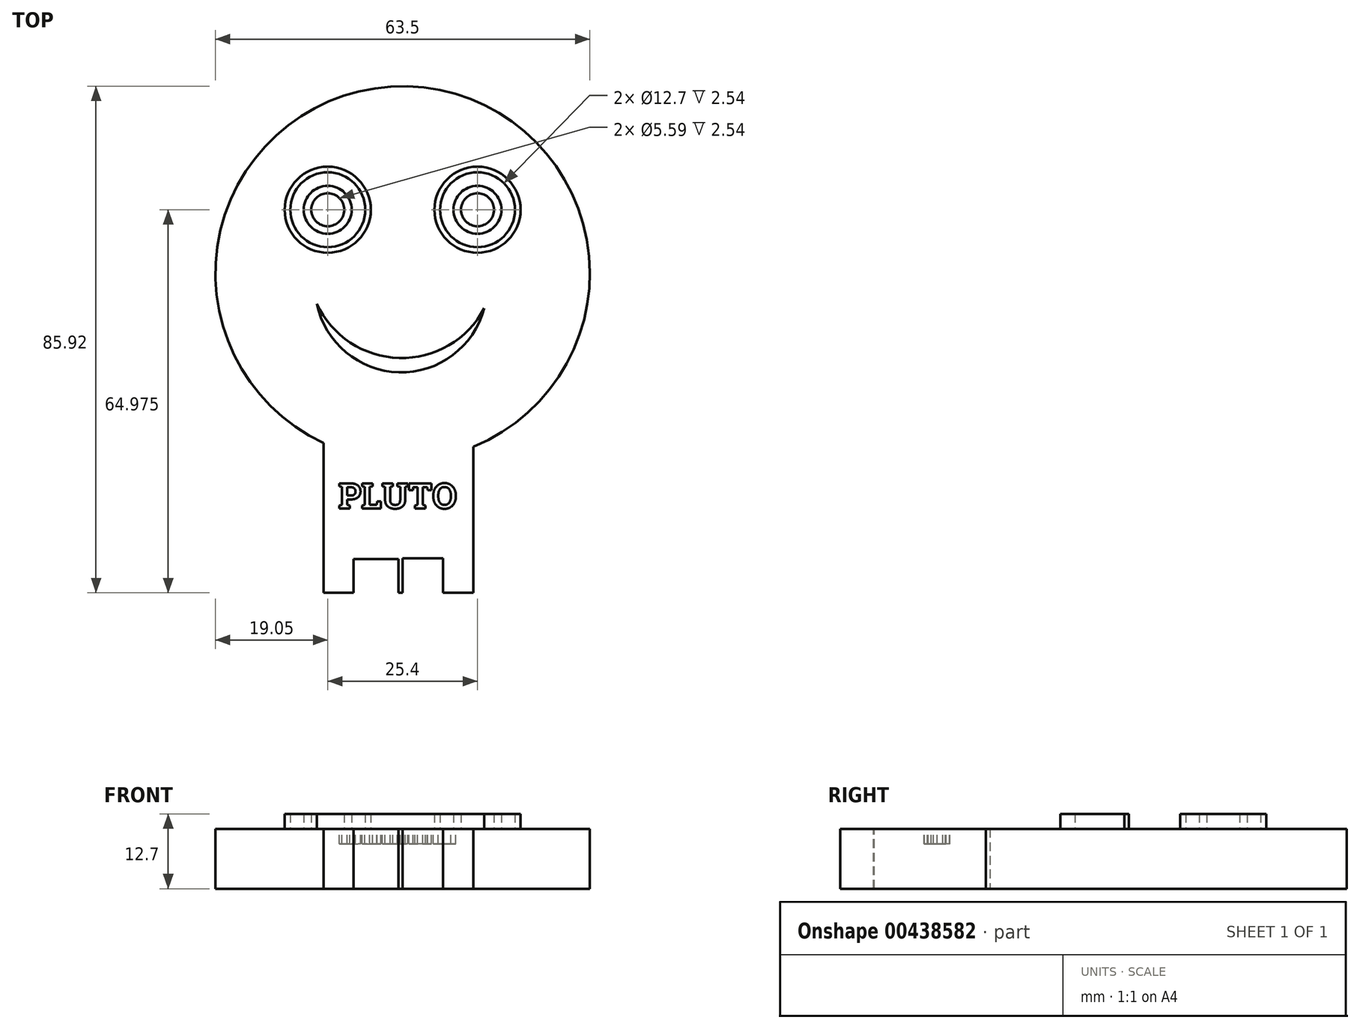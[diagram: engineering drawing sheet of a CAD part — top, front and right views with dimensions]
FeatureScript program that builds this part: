
annotation { "Feature Type Name" : "Feature", "Feature Type Description" : "" }
export const myFeature = defineFeature(function(context is Context, id is Id, definition is map)
    precondition{}
    {
        {
            var Q0;
            Q0=qCreatedBy(makeId("Top.planeOp"),FACE);
            var sketch = newSketch(context, id + "F0", { "sketchPlane" : qUnion([Q0])});
            skCircle(sketch, "E0", {"center": v(0, 20.55) * mm, "radius": 31.75 * mm});
            skLineSegment(sketch, "E1.bottom", {"start": v(-13.44, -8.22) * mm, "end": v(11.96, -8.22) * mm});
            skLineSegment(sketch, "E1.top", {"start": v(-13.44, -33.62) * mm, "end": v(11.96, -33.62) * mm});
            skLineSegment(sketch, "E1.left", {"start": v(-13.44, -8.22) * mm, "end": v(-13.44, -33.62) * mm});
            skLineSegment(sketch, "E1.right", {"start": v(11.96, -8.22) * mm, "end": v(11.96, -33.62) * mm});
            skSolve(sketch);
        }
        {
            var Q0;
            {var subQ0=sQuery(id+"F0.wireOp",EDGE,"E1.bottom");Q0=makeQuery(id+"F0.imprint","IMPRINT",FACE,{"disambiguationData":[TD([[makeQuery(id+"F0.imprint","IMPRINT",EDGE,{"derivedFrom":subQ0}),-1.0]])]});}
            var Q1;
            {var subQ4=sQuery(id+"F0.wireOp",EDGE,"E1.top");Q1=makeQuery(id+"F0.imprint","IMPRINT",FACE,{"disambiguationData":[TD([[makeQuery(id+"F0.imprint","IMPRINT",EDGE,{"derivedFrom":subQ4}),1.0]])]});}
            var Q2;
            {var subQ0=sQuery(id+"F0.wireOp",EDGE,"E1.bottom");Q2=makeQuery(id+"F0.imprint","IMPRINT",FACE,{"disambiguationData":[TD([[makeQuery(id+"F0.imprint","IMPRINT",EDGE,{"derivedFrom":subQ0}),1.0]])]});}
            extrude(context, id + "F1", {"entities" : qUnion([Q0, Q1, Q2]), "depth" : 10.16 * mm});
        }
        {
            var Q0;
            Q0=makeQuery(id+"F1.opExtrude","CAP_FACE",FACE,{"disambiguationData":[OSD([sQuery(id+"F0.wireOp",EDGE,"E0"),sQuery(id+"F0.wireOp",EDGE,"E1.top"),sQuery(id+"F0.wireOp",EDGE,"E1.left"),sQuery(id+"F0.wireOp",EDGE,"E1.right")])],"isStart":false});
            var sketch = newSketch(context, id + "F2", { "sketchPlane" : qUnion([Q0])});
            skCircle(sketch, "E2", {"center": v(-12.7, 31.35) * mm, "radius": 6.35 * mm});
            skCircle(sketch, "E3", {"center": v(12.7, 31.35) * mm, "radius": 6.35 * mm});
            skArc(sketch, "E4", {"start": v(-14.54, 15.4) * mm, "mid": v(-0.65, 3.78) * mm, "end": v(13.85, 14.63) * mm});
            skLineSegment(sketch, "E5", {"start": v(-12.7, 31.35) * mm, "end": v(0, 31.35) * mm, "construction": true});
            skLineSegment(sketch, "E6", {"start": v(0, 31.35) * mm, "end": v(12.7, 31.35) * mm, "construction": true});
            skCircle(sketch, "E7", {"center": v(-12.7, 31.35) * mm, "radius": 7.3 * mm});
            skCircle(sketch, "E8", {"center": v(12.7, 31.35) * mm, "radius": 7.3 * mm});
            skArc(sketch, "E9", {"start": v(-14.54, 15.4) * mm, "mid": v(-0.58, 6.21) * mm, "end": v(13.85, 14.63) * mm});
            skSolve(sketch);
        }
        {
            var Q0;
            Q0=makeQuery(id+"F2.imprint","IMPRINT",FACE,{"disambiguationData":[TD([[makeQuery(id+"F2.imprint","IMPRINT",EDGE,{"derivedFrom":sQuery(id+"F2.wireOp",EDGE,"E2")}),-1.0]])]});
            var Q1;
            Q1=makeQuery(id+"F2.imprint","IMPRINT",FACE,{"disambiguationData":[TD([[makeQuery(id+"F2.imprint","IMPRINT",EDGE,{"derivedFrom":sQuery(id+"F2.wireOp",EDGE,"E4")}),1.0]])]});
            var Q2;
            Q2=makeQuery(id+"F2.imprint","IMPRINT",FACE,{"disambiguationData":[TD([[makeQuery(id+"F2.imprint","IMPRINT",EDGE,{"derivedFrom":sQuery(id+"F2.wireOp",EDGE,"E3")}),-1.0]])]});
            var Q3;
            Q3=sQuery(id+"F2.wireOp",EDGE,"E2");
            var Q4;
            Q4=sQuery(id+"F2.wireOp",EDGE,"E7");
            extrude(context, id + "F3", {"entities" : qUnion([Q0, Q1, Q2]), "operationType" : NewBodyOperationType.ADD, "surfaceEntities" : qUnion([Q3, Q4]), "depth" : 2.54 * mm});
        }
        {
            var Q0;
            Q0=makeQuery(id+"F1.opExtrude","CAP_FACE",FACE,{"disambiguationData":[OSD([sQuery(id+"F0.wireOp",EDGE,"E0"),sQuery(id+"F0.wireOp",EDGE,"E1.top"),sQuery(id+"F0.wireOp",EDGE,"E1.left"),sQuery(id+"F0.wireOp",EDGE,"E1.right")])],"isStart":false});
            var sketch = newSketch(context, id + "F4", { "sketchPlane" : qUnion([Q0])});
            skCircle(sketch, "E10", {"center": v(-12.7, 31.35) * mm, "radius": 2.8 * mm});
            skCircle(sketch, "E11", {"center": v(12.7, 31.35) * mm, "radius": 2.8 * mm});
            skLineSegment(sketch, "E12", {"start": v(-12.7, 31.35) * mm, "end": v(0, 31.35) * mm, "construction": true});
            skLineSegment(sketch, "E13", {"start": v(12.7, 31.35) * mm, "end": v(0, 31.35) * mm, "construction": true});
            skCircle(sketch, "E14", {"center": v(-12.7, 31.35) * mm, "radius": 4.06 * mm});
            skCircle(sketch, "E15", {"center": v(12.7, 31.35) * mm, "radius": 4.06 * mm});
            skSolve(sketch);
        }
        {
            var Q0;
            Q0=makeQuery(id+"F4.imprint","IMPRINT",FACE,{"disambiguationData":[TD([[makeQuery(id+"F4.imprint","IMPRINT",EDGE,{"derivedFrom":sQuery(id+"F4.wireOp",EDGE,"E10")}),-1.0]])]});
            var Q1;
            Q1=makeQuery(id+"F4.imprint","IMPRINT",FACE,{"disambiguationData":[TD([[makeQuery(id+"F4.imprint","IMPRINT",EDGE,{"derivedFrom":sQuery(id+"F4.wireOp",EDGE,"E11")}),-1.0]])]});
            extrude(context, id + "F5", {"entities" : qUnion([Q0, Q1]), "operationType" : NewBodyOperationType.ADD, "depth" : 2.54 * mm});
        }
        {
            var Q0;
            Q0=makeQuery(id+"F1.opExtrude","CAP_FACE",FACE,{"disambiguationData":[OSD([sQuery(id+"F0.wireOp",EDGE,"E0"),sQuery(id+"F0.wireOp",EDGE,"E1.top"),sQuery(id+"F0.wireOp",EDGE,"E1.left"),sQuery(id+"F0.wireOp",EDGE,"E1.right")])],"isStart":false});
            var sketch = newSketch(context, id + "F6", { "sketchPlane" : qUnion([Q0])});
            skPoint(sketch, "E16.oppositeSnap0", {"position": v(-0.74, -33.62) * mm});
            skLineSegment(sketch, "E16.bottom", {"start": v(-8.34, -27.92) * mm, "end": v(-0.74, -27.92) * mm});
            skLineSegment(sketch, "E16.top", {"start": v(-8.34, -46.63) * mm, "end": v(-0.74, -46.63) * mm});
            skLineSegment(sketch, "E16.left", {"start": v(-8.34, -27.92) * mm, "end": v(-8.34, -46.63) * mm});
            skLineSegment(sketch, "E16.right", {"start": v(-0.74, -27.92) * mm, "end": v(-0.74, -46.63) * mm});
            skLineSegment(sketch, "E17.bottom", {"start": v(0, -47.09) * mm, "end": v(6.88, -47.09) * mm});
            skLineSegment(sketch, "E17.top", {"start": v(0, -27.8) * mm, "end": v(6.88, -27.8) * mm});
            skLineSegment(sketch, "E17.left", {"start": v(0, -47.09) * mm, "end": v(0, -27.8) * mm});
            skLineSegment(sketch, "E17.right", {"start": v(6.88, -47.09) * mm, "end": v(6.88, -27.8) * mm});
            skSolve(sketch);
        }
        {
            var Q0;
            Q0 = qSketchRegion(id + "F6", true);
            extrude(context, id + "F7", {"entities" : qUnion([Q0]), "operationType" : NewBodyOperationType.REMOVE, "oppositeDirection" : true, "depth" : 25.4 * mm});
        }
        {
            var Q0;
            Q0=makeQuery(id+"F1.opExtrude","CAP_FACE",FACE,{"disambiguationData":[OSD([sQuery(id+"F0.wireOp",EDGE,"E0"),sQuery(id+"F0.wireOp",EDGE,"E1.top"),sQuery(id+"F0.wireOp",EDGE,"E1.left"),sQuery(id+"F0.wireOp",EDGE,"E1.right")])],"isStart":false});
            var sketch = newSketch(context, id + "F8", { "sketchPlane" : qUnion([Q0])});
            skLineSegment(sketch, "E18.bottom", {"start": v(-10.9, -15.02) * mm, "end": v(9.42, -9.16) * mm, "construction": true});
            skLineSegment(sketch, "E18.top", {"start": v(-10.9, -25.18) * mm, "end": v(9.42, -19.32) * mm, "construction": true});
            skLineSegment(sketch, "E18.left", {"start": v(-10.9, -15.02) * mm, "end": v(-10.9, -25.18) * mm, "construction": true});
            skLineSegment(sketch, "E18.right", {"start": v(9.42, -9.16) * mm, "end": v(9.42, -19.32) * mm, "construction": true});
            skText(sketch, "E19", { "text": "PLUTO", "fontName": "RobotoSlab-Bold.ttf"});
            const initialGuessF8  = {"E19": [-0.0109, -0.01932, 1, 0, 0.0043]};
            skSetInitialGuess(sketch, initialGuessF8);
            skSolve(sketch);
        }
        {
            var Q0;
            Q0 = qSketchRegion(id + "F8", true);
            extrude(context, id + "F9", {"entities" : qUnion([Q0]), "operationType" : NewBodyOperationType.REMOVE, "oppositeDirection" : true, "depth" : 2.54 * mm});
        }
    });
